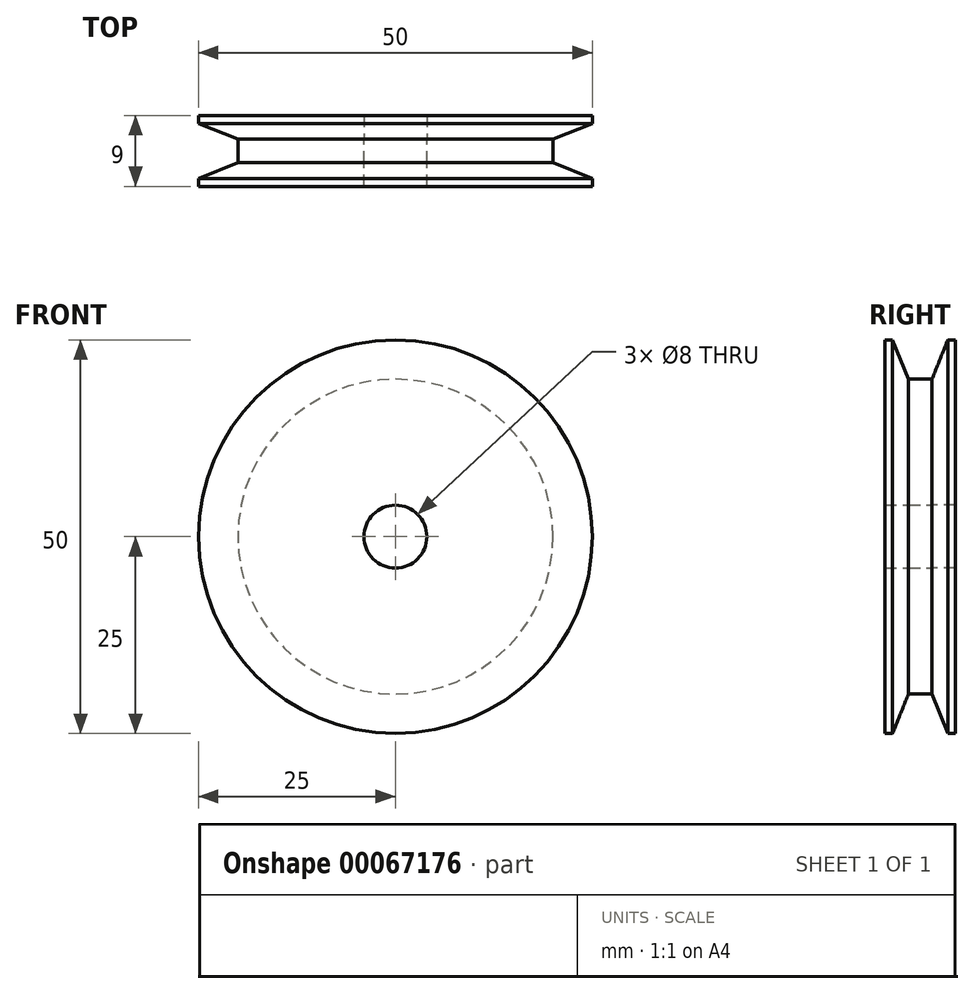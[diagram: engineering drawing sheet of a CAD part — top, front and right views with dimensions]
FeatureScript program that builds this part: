
annotation { "Feature Type Name" : "Feature", "Feature Type Description" : "" }
export const myFeature = defineFeature(function(context is Context, id is Id, definition is map)
    precondition{}
    {
        {
            var Q0;
            Q0=qCreatedBy(makeId("Front.planeOp"),FACE);
            var sketch = newSketch(context, id + "F0", { "sketchPlane" : qUnion([Q0])});
            skCircle(sketch, "E0", {"center": v(0, 0) * mm, "radius": 20 * mm});
            skCircle(sketch, "E1", {"center": v(0, 0) * mm, "radius": 4 * mm});
            skSolve(sketch);
        }
        {
            var Q0;
            Q0=makeQuery(id+"F0.imprint","IMPRINT",FACE,{"disambiguationData":[TD([[makeQuery(id+"F0.imprint","IMPRINT",EDGE,{"derivedFrom":sQuery(id+"F0.wireOp",EDGE,"E0")}),1.0]])]});
            extrude(context, id + "F1", {"entities" : qUnion([Q0]), "depth" : 3 * mm});
        }
        {
            var Q0;
            Q0=makeQuery(id+"F1.opExtrude","CAP_FACE",FACE,{"disambiguationData":[OSD([sQuery(id+"F0.wireOp",EDGE,"E0"),sQuery(id+"F0.wireOp",EDGE,"E1")])],"isStart":true});
            var sketch = newSketch(context, id + "F2", { "sketchPlane" : qUnion([Q0])});
            skCircle(sketch, "E2", {"center": v(0, 0) * mm, "radius": 25 * mm});
            skSolve(sketch);
        }
        {
            var Q0;
            Q0=makeQuery(id+"F2.imprint","IMPRINT",FACE,{"disambiguationData":[TD([[makeQuery(id+"F2.imprint","IMPRINT",EDGE,{"derivedFrom":sQuery(id+"F2.wireOp",EDGE,"E2")}),1.0]])]});
            var Q1;
            Q1=makeQuery(id+"F2.imprint","IMPRINT",FACE,{"disambiguationData":[TD([[makeQuery(id+"F2.imprint","IMPRINT",EDGE,{"derivedFrom":makeQuery(id+"F1.opExtrude","CAP_EDGE",EDGE,{"disambiguationData":[OSD([sQuery(id+"F0.wireOp",EDGE,"E0")])],"isStart":true})}),-1.0]])]});
            extrude(context, id + "F3", {"entities" : qUnion([Q0, Q1]), "depth" : 3 * mm});
        }
        {
            var Q0;
            Q0=makeQuery(id+"F1.opExtrude","CAP_FACE",FACE,{"disambiguationData":[OSD([sQuery(id+"F0.wireOp",EDGE,"E0"),sQuery(id+"F0.wireOp",EDGE,"E1")])],"isStart":false});
            var sketch = newSketch(context, id + "F4", { "sketchPlane" : qUnion([Q0])});
            skCircle(sketch, "E3", {"center": v(0, 0) * mm, "radius": 25 * mm});
            skSolve(sketch);
        }
        {
            var Q0;
            Q0=makeQuery(id+"F4.imprint","IMPRINT",FACE,{"disambiguationData":[TD([[makeQuery(id+"F4.imprint","IMPRINT",EDGE,{"derivedFrom":makeQuery(id+"F1.opExtrude","CAP_EDGE",EDGE,{"disambiguationData":[OSD([sQuery(id+"F0.wireOp",EDGE,"E0")])],"isStart":false})}),1.0]])]});
            var Q1;
            Q1=makeQuery(id+"F4.imprint","IMPRINT",FACE,{"disambiguationData":[TD([[makeQuery(id+"F4.imprint","IMPRINT",EDGE,{"derivedFrom":sQuery(id+"F4.wireOp",EDGE,"E3")}),1.0]])]});
            extrude(context, id + "F5", {"entities" : qUnion([Q0, Q1]), "depth" : 3 * mm});
        }
        {
            var Q0;
            Q0=makeQuery(id+"F3.opExtrude","CAP_EDGE",EDGE,{"disambiguationData":[OSD([sQuery(id+"F2.wireOp",EDGE,"E2")])],"isStart":true});
            var Q1;
            Q1=makeQuery(id+"F5.opExtrude","CAP_EDGE",EDGE,{"disambiguationData":[OSD([sQuery(id+"F4.wireOp",EDGE,"E3")])],"isStart":true});
            chamfer(context, id + "F6", {"entities" : qUnion([Q0, Q1]), "chamferType" : ChamferType.TWO_OFFSETS, "width1" : 2 * mm, "oppositeDirection" : false, "width2" : 5 * mm, "tangentPropagation" : true});
        }
    });
